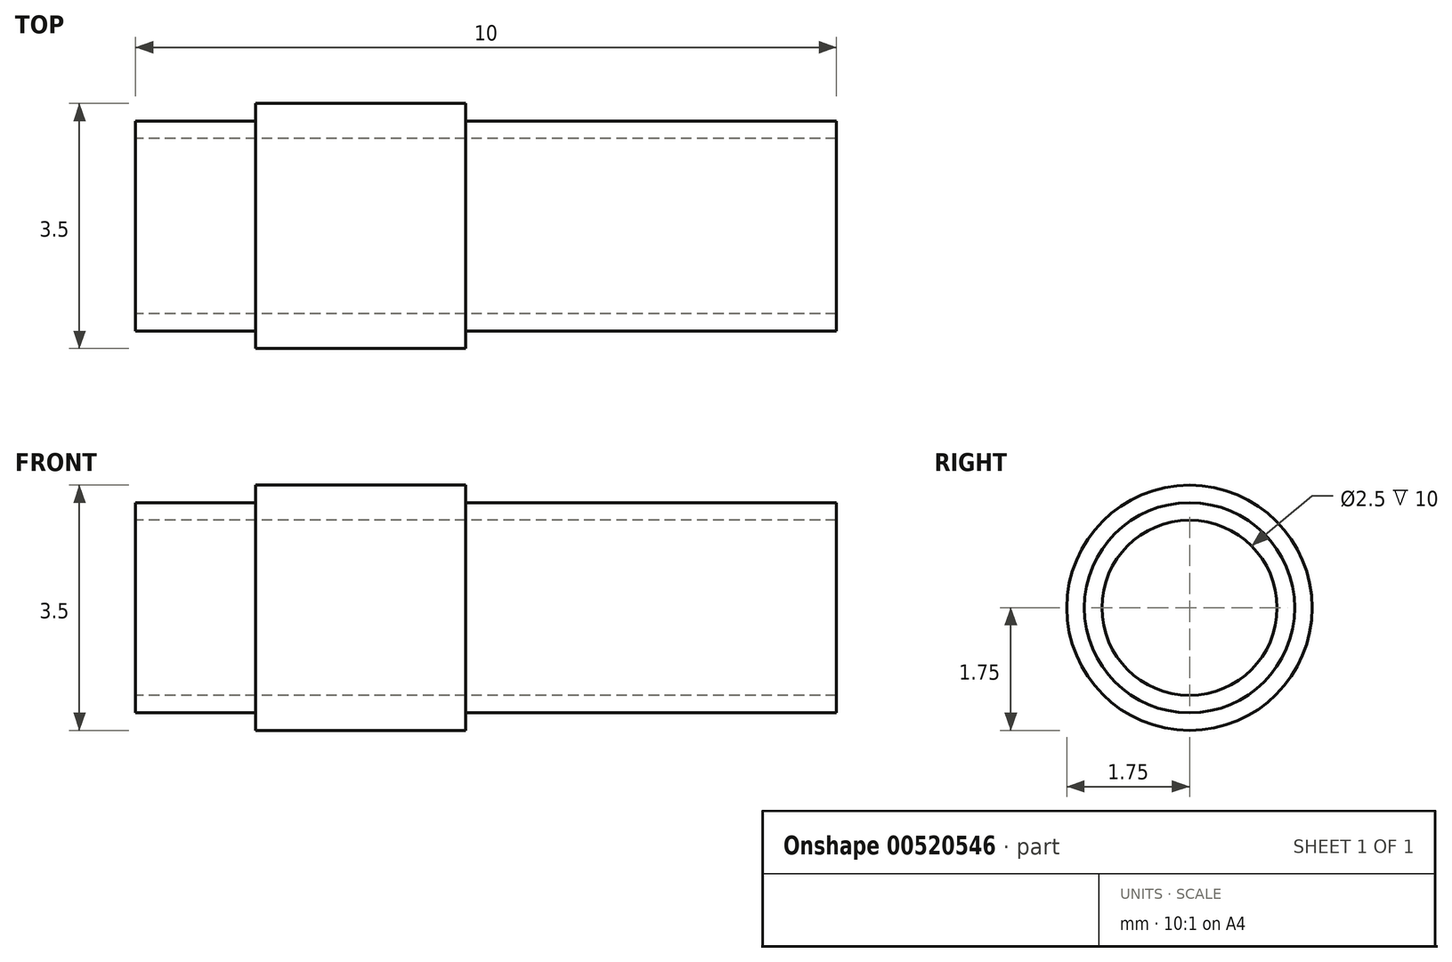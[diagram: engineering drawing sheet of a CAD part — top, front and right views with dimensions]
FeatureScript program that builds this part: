
annotation { "Feature Type Name" : "Feature", "Feature Type Description" : "" }
export const myFeature = defineFeature(function(context is Context, id is Id, definition is map)
    precondition{}
    {
        {
            var Q0;
            Q0=qCreatedBy(makeId("Right.planeOp"),FACE);
            var sketch = newSketch(context, id + "F0", { "sketchPlane" : qUnion([Q0])});
            skCircle(sketch, "E0", {"center": v(0, 0) * mm, "radius": 1.25 * mm});
            skCircle(sketch, "E1", {"center": v(0, 0) * mm, "radius": 1.5 * mm});
            skSolve(sketch);
        }
        {
            var Q0;
            Q0 = qSketchRegion(id + "F0", true);
            extrude(context, id + "F1", {"entities" : qUnion([Q0]), "depth" : 10 * mm, "offsetDistance" : 25 * mm});
        }
        {
            var Q0;
            Q0=qCreatedBy(makeId("Right.planeOp"),FACE);
            cPlane(context, id + "F2", {"entities" : qUnion([Q0]), "cplaneType" : CPlaneType.OFFSET, "offset" : 1.71 * mm, "width" : 150 * mm, "height" : 150 * mm});
        }
        {
            var Q0;
            Q0=qCreatedBy(id+"F2.planeOp",FACE);
            var sketch = newSketch(context, id + "F3", { "sketchPlane" : qUnion([Q0])});
            skCircle(sketch, "E2", {"center": v(0, 0) * mm, "radius": 1.5 * mm});
            skCircle(sketch, "E3", {"center": v(0, 0) * mm, "radius": 1.75 * mm});
            skSolve(sketch);
        }
        {
            var Q0;
            Q0 = qSketchRegion(id + "F3", true);
            extrude(context, id + "F4", {"entities" : qUnion([Q0]), "operationType" : NewBodyOperationType.ADD, "depth" : 3 * mm, "offsetDistance" : 25 * mm});
        }
    });
